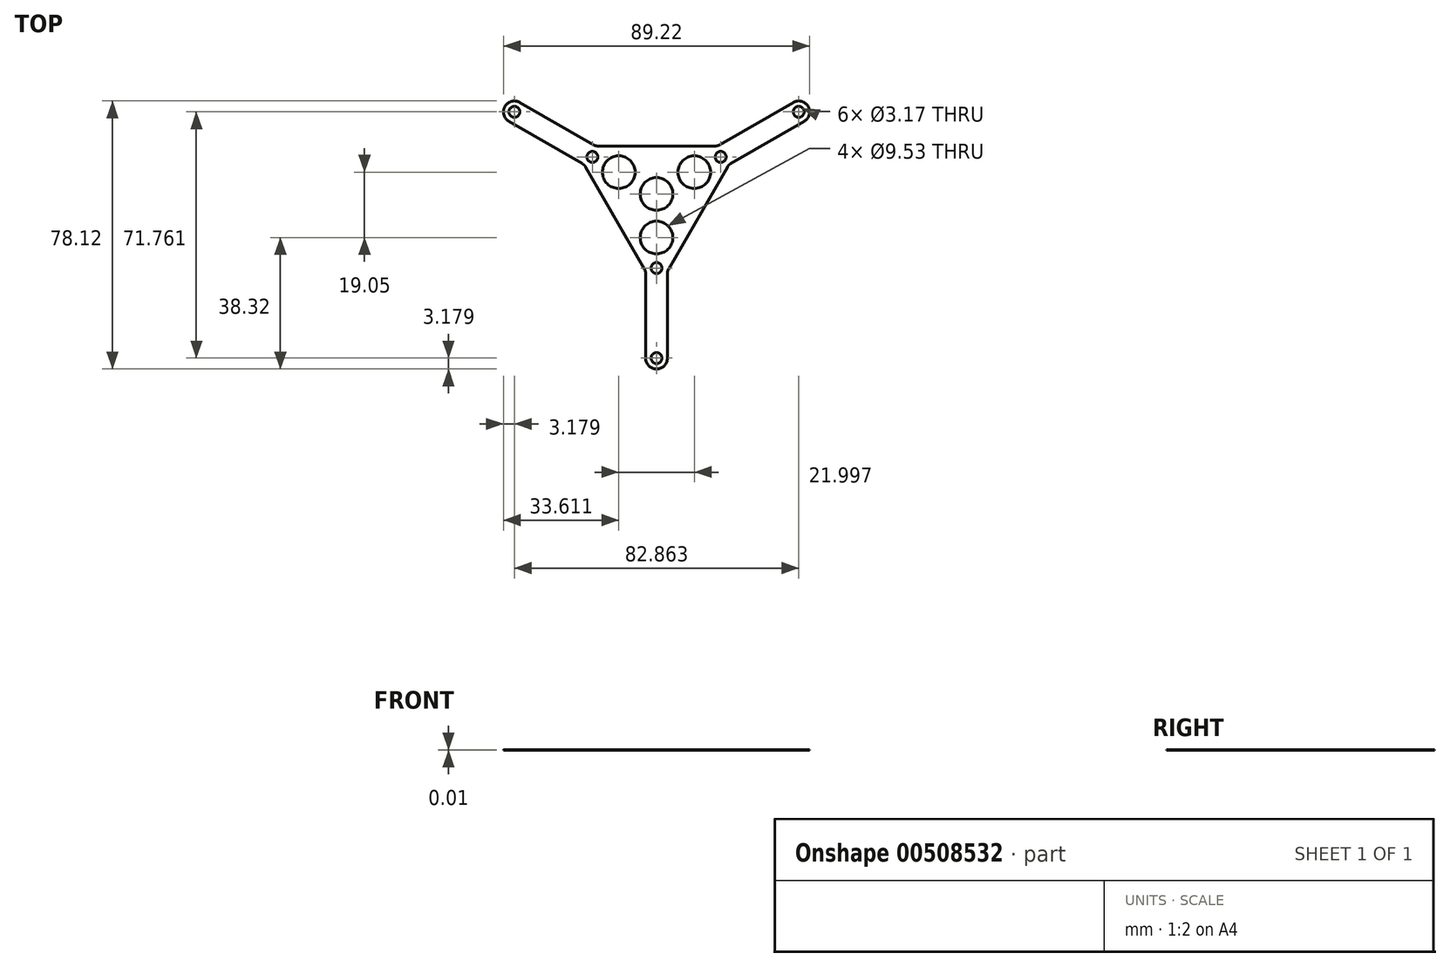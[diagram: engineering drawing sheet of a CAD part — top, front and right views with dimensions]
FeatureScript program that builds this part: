
annotation { "Feature Type Name" : "Feature", "Feature Type Description" : "" }
export const myFeature = defineFeature(function(context is Context, id is Id, definition is map)
    precondition{}
    {
        {
            var Q0;
            Q0=qCreatedBy(makeId("Top.planeOp"),FACE);
            var sketch = newSketch(context, id + "F0", { "sketchPlane" : qUnion([Q0])});
            skCircle(sketch, "E0.cCircle", {"center": v(0, 0) * mm, "radius": 27.94 * mm, "construction": true});
            skLineSegment(sketch, "E0.0", {"start": v(0, -27.94) * mm, "end": v(-24.2, 13.97) * mm});
            skLineSegment(sketch, "E0.1", {"start": v(-24.2, 13.97) * mm, "end": v(24.2, 13.97) * mm});
            skLineSegment(sketch, "E0.2", {"start": v(24.2, 13.97) * mm, "end": v(0, -27.94) * mm});
            skCircle(sketch, "E1.cCircle", {"center": v(0, 0) * mm, "radius": 12.7 * mm, "construction": true});
            skLineSegment(sketch, "E1.0", {"start": v(0, -12.7) * mm, "end": v(-11, 6.35) * mm, "construction": true});
            skLineSegment(sketch, "E1.1", {"start": v(-11, 6.35) * mm, "end": v(11, 6.35) * mm, "construction": true});
            skLineSegment(sketch, "E1.2", {"start": v(11, 6.35) * mm, "end": v(0, -12.7) * mm, "construction": true});
            skCircle(sketch, "E2.cCircle", {"center": v(0, 0) * mm, "radius": 21.59 * mm, "construction": true});
            skLineSegment(sketch, "E2.0", {"start": v(0, -21.6) * mm, "end": v(-18.7, 10.8) * mm, "construction": true});
            skLineSegment(sketch, "E2.1", {"start": v(-18.7, 10.8) * mm, "end": v(18.7, 10.8) * mm, "construction": true});
            skLineSegment(sketch, "E2.2", {"start": v(18.7, 10.8) * mm, "end": v(0, -21.6) * mm, "construction": true});
            skCircle(sketch, "E3", {"center": v(11, 6.35) * mm, "radius": 4.76 * mm});
            skCircle(sketch, "E4", {"center": v(0, -12.7) * mm, "radius": 4.76 * mm});
            skCircle(sketch, "E5", {"center": v(-11, 6.35) * mm, "radius": 4.76 * mm});
            skCircle(sketch, "E6", {"center": v(18.7, 10.8) * mm, "radius": 1.59 * mm});
            skCircle(sketch, "E7", {"center": v(0, -21.59) * mm, "radius": 1.59 * mm});
            skCircle(sketch, "E8", {"center": v(-18.7, 10.8) * mm, "radius": 1.59 * mm});
            skCircle(sketch, "E9", {"center": v(0, 0) * mm, "radius": 4.76 * mm});
            skLineSegment(sketch, "E10", {"start": v(-3.18, -22.44) * mm, "end": v(-3.18, -47.84) * mm});
            skLineSegment(sketch, "E11", {"start": v(3.17, -47.84) * mm, "end": v(3.17, -22.44) * mm});
            skArc(sketch, "E12", {"start": v(-3.18, -47.84) * mm, "mid": v(0, -51.02) * mm, "end": v(3.17, -47.84) * mm});
            skCircle(sketch, "E13", {"center": v(0, -47.84) * mm, "radius": 1.59 * mm});
            skLineSegment(sketch, "E14.1.0", {"start": v(21.02, 8.47) * mm, "end": v(43.02, 21.17) * mm});
            skCircle(sketch, "E14.1.1", {"center": v(41.43, 23.92) * mm, "radius": 1.59 * mm});
            skLineSegment(sketch, "E14.1.2", {"start": v(39.84, 26.67) * mm, "end": v(17.85, 13.97) * mm});
            skArc(sketch, "E14.1.3", {"start": v(43.02, 21.17) * mm, "mid": v(44.18, 25.5) * mm, "end": v(39.84, 26.67) * mm});
            skLineSegment(sketch, "E14.2.0", {"start": v(-17.85, 13.97) * mm, "end": v(-39.84, 26.67) * mm});
            skCircle(sketch, "E14.2.1", {"center": v(-41.43, 23.92) * mm, "radius": 1.59 * mm});
            skLineSegment(sketch, "E14.2.2", {"start": v(-43.02, 21.17) * mm, "end": v(-21.02, 8.47) * mm});
            skArc(sketch, "E14.2.3", {"start": v(-39.84, 26.67) * mm, "mid": v(-44.18, 25.5) * mm, "end": v(-43.02, 21.17) * mm});
            skLineSegment(sketch, "E15", {"start": v(-41.43, 23.92) * mm, "end": v(0, -47.84) * mm, "construction": true});
            skLineSegment(sketch, "E16", {"start": v(0, -47.84) * mm, "end": v(41.43, 23.92) * mm, "construction": true});
            skLineSegment(sketch, "E17", {"start": v(41.43, 23.92) * mm, "end": v(-41.43, 23.92) * mm, "construction": true});
            skSolve(sketch);
        }
        {
            var Q0;
            Q0=qSketchRegion(id+"F0",true);
            extrude(context, id + "F1", {"entities" : qUnion([Q0]), "depth" : 1 / 101.6 * mm});
        }
        {
            var Q0;
            Q0=makeQuery(id+"F1.opExtrude","SWEPT_EDGE",EDGE,{"disambiguationData":[OSD([sQuery(id+"F0.wireOp",EDGE,"E0.0"),sQuery(id+"F0.wireOp",EDGE,"E0.1")])]});
            var Q1;
            Q1=makeQuery(id+"F1.opExtrude","SWEPT_EDGE",EDGE,{"disambiguationData":[OSD([sQuery(id+"F0.wireOp",EDGE,"E0.0"),sQuery(id+"F0.wireOp",EDGE,"E0.2")])]});
            var Q2;
            Q2=makeQuery(id+"F1.opExtrude","SWEPT_EDGE",EDGE,{"disambiguationData":[OSD([sQuery(id+"F0.wireOp",EDGE,"E0.1"),sQuery(id+"F0.wireOp",EDGE,"E0.2")])]});
            fillet(context, id + "F2", {"entities" : qUnion([Q0, Q1, Q2]), "radius" : 2.54 * mm, "tangentPropagation" : true, "allowEdgeOverflow" : false});
        }
    });
